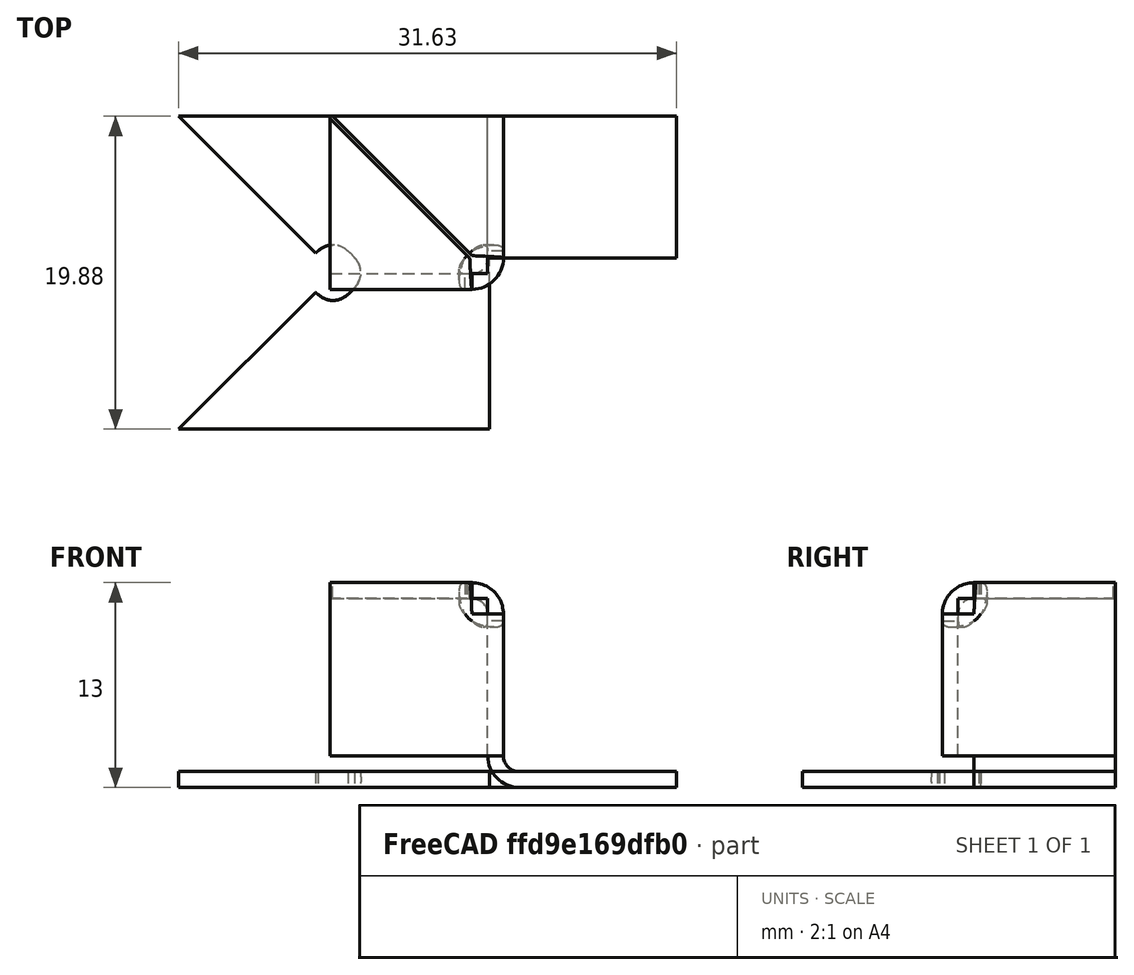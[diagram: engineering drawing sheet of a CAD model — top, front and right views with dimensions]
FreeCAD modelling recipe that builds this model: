
FCSTD DOCUMENT  (FreeCAD 0.19R23069 (Git))
Label: CornerRelief_test_none_native_SMWB
License: All rights reserved
LicenseURL: http://en.wikipedia.org/wiki/All_rights_reserved
objects: Part::FeaturePython×5, Sketcher::SketchObject×4, Part::Box×1, Part::Fillet×1, Part::Offset×1, Part::Feature×1, App::Part×1
note: 13 computed .brp shape members not serialized (recipe doc carries the construction recipe); baked Part::Feature solids carry a one-line shape summary decoded from their .brp

FEATURE [Part::Box] Box  label="Cube"
  AttacherType = Attacher::AttachEngine3D
  Height = 10
  Length = 10
  Width = 10
FEATURE [Part::FeaturePython] Relief  # WARN: FeaturePython — macro-defined, semantics opaque (R4)
  baseObject = -> Box [Vertex5]
  relief = 1
FEATURE [Sketcher::SketchObject] Sketch
  ExternalGeometry = -> [Relief]
  MapMode = 5
  Placement = pos=(0,0,10) rot=(0,0,1;0rad)
  Support = -> [Relief]
  sketch-geometry (7):
    g0: LineSegment [constr] StartX=9 StartY=1 StartZ=0 EndX=-4e-16 EndY=10 EndZ=0
    g1: LineSegment [constr] StartX=-0.0707107 StartY=9.92929 StartZ=0 EndX=0.0707107 EndY=10.0707 EndZ=0
    g2: LineSegment StartX=0.0707107 StartY=10.0707 StartZ=0 EndX=9.07071 EndY=1.07071 EndZ=0
    g3: LineSegment [constr] StartX=9.07071 StartY=1.07071 StartZ=0 EndX=8.92929 EndY=0.929289 EndZ=0
    g4: LineSegment StartX=8.92929 StartY=0.929289 StartZ=0 EndX=-0.0707107 EndY=9.92929 EndZ=0
    g5: ArcOfCircle CenterX=9 CenterY=1 CenterZ=0 NormalX=0 NormalY=0 NormalZ=1 AngleXU=0 Radius=0.1 StartAngle=3.92699 EndAngle=7.06858
    g6: ArcOfCircle CenterX=0 CenterY=10 CenterZ=0 NormalX=0 NormalY=0 NormalZ=1 AngleXU=0 Radius=0.1 StartAngle=0.785398 EndAngle=3.92699
  constraints (15):
    c: Coincident(g0,g-3)
    c: Coincident(g0,g-4)
    c: Perpendicular(g1,g2) = 4.71239
    c: Perpendicular(g2,g3) = 4.71239
    c: Perpendicular(g3,g4) = 4.71239
    c: Coincident(g1,g4)
    c: Symmetric(g1,g1,g0)
    c: Symmetric(g3,g3,g0)
    c: Distance(g1) = 0.2
    c: Coincident(g5,g0)
    c: Coincident(g5,g3)
    c: Coincident(g5,g2)
    c: Coincident(g6,g0)
    c: Coincident(g6,g1)
    c: Coincident(g6,g1)
FEATURE [Part::FeaturePython] XOR  # WARN: FeaturePython — macro-defined, semantics opaque (R4)
  Objects = -> [Sketch,Relief]
  Tolerance = 0
FEATURE [Part::FeaturePython] Facebinder  # WARN: FeaturePython — macro-defined, semantics opaque (R4)
  Area = 294.457
  Extrusion = 0
  Faces = -> [XOR]
  RemoveSplitter = false
  Sew = false
FEATURE [Part::Fillet] Fillet
  Base = -> Facebinder
  Edges = 3 edges r=1: [Edge2,Edge9,Edge11]
FEATURE [Part::Offset] Offset
  Fill = true
  Intersection = false
  Join = 0
  Mode = 0
  SelfIntersection = false
  Source = -> Fillet
  Value = 1
FEATURE [Part::FeaturePython] CornerRelief  # WARN: FeaturePython — macro-defined, semantics opaque (R4)
  ReliefSketch = 0
  Size = 2
  SizeRatio = 1.5
  XOffset = 0
  YOffset = 0
  baseObject = -> Offset [Edge49,Edge51]
  kfactor = 0.5
FEATURE [Part::FeaturePython] Bend  # WARN: FeaturePython — macro-defined, semantics opaque (R4)
  AutoMiter = true
  BendType = 0
  LengthList = [10]
  ReliefFactor = 0.7
  UseReliefFactor = false
  angle = 90
  baseObject = -> CornerRelief [Edge30]
  bendAList = [90]
  extend1 = 0
  extend2 = 0
  gap1 = 0
  gap2 = 0
  invert = false
  kfactor = 0.5
  length = 10
  miterangle1 = 0
  miterangle2 = 0
  offset = 0
  radius = 1
  reliefType = 0
  reliefd = 1
  reliefw = 0.8
  sketchflip = false
  sketchinvert = false
  unfold = false
FEATURE [Part::Feature] Unfold
  shape: bbox 31.63 x 19.89 x 1.1 mm, 17 faces (baked)
FEATURE [Sketcher::SketchObject] Unfold_Sketch
  sketch-geometry (15):
    g0: ArcOfCircle CenterX=0.408186 CenterY=0.293142 CenterZ=0 NormalX=0 NormalY=0 NormalZ=1 AngleXU=1.5708 Radius=2 StartAngle=2.40622 EndAngle=2.51171
    g1: LineSegment StartX=-0.933548 StartY=-1.19001 StartZ=0 EndX=-9.62849 EndY=-9.88496 EndZ=0
    g2: BSplineCurve PolesCount=15 KnotsCount=13 Degree=3 IsPeriodic=0
    g3: ArcOfCircle CenterX=-0.0630528 CenterY=0.293142 CenterZ=0 NormalX=0 NormalY=0 NormalZ=1 AngleXU=1.5708 Radius=2 StartAngle=3.77147 EndAngle=4.08251
    g4: BSplineCurve PolesCount=15 KnotsCount=13 Degree=3 IsPeriodic=0
    g5: ArcOfCircle CenterX=-0.0630528 CenterY=-0.178097 CenterZ=0 NormalX=0 NormalY=0 NormalZ=1 AngleXU=1.5708 Radius=2 StartAngle=5.34227 EndAngle=5.6533
    g6: BSplineCurve PolesCount=15 KnotsCount=13 Degree=3 IsPeriodic=0
    g7: BSplineCurve PolesCount=15 KnotsCount=13 Degree=3 IsPeriodic=0
    g8: ArcOfCircle CenterX=0.408186 CenterY=-0.178097 CenterZ=0 NormalX=0 NormalY=0 NormalZ=1 AngleXU=1.5708 Radius=2 StartAngle=0.629881 EndAngle=0.735377
    g9: LineSegment StartX=-9.62849 StartY=10 StartZ=0 EndX=-0.933548 EndY=1.30506 EndZ=0
    g10: LineSegment StartX=10.115 StartY=-9.88496 StartZ=0 EndX=-9.62849 EndY=-9.88496 EndZ=0
    g11: LineSegment StartX=10.115 StartY=-9.88496 StartZ=0 EndX=10.115 EndY=1 EndZ=0
    g12: LineSegment StartX=10.115 StartY=1 StartZ=0 EndX=22 EndY=1 EndZ=0
    g13: LineSegment StartX=22 StartY=1 StartZ=0 EndX=22 EndY=10 EndZ=0
    g14: LineSegment StartX=22 StartY=10 StartZ=0 EndX=-9.62849 EndY=10 EndZ=0
FEATURE [Sketcher::SketchObject] Unfold_Sketch_Outline
  sketch-geometry (15):
    g0: LineSegment StartX=10.115 StartY=-9.88496 StartZ=0 EndX=-9.62849 EndY=-9.88496 EndZ=0
    g1: LineSegment StartX=-0.933548 StartY=-1.19001 StartZ=0 EndX=-9.62849 EndY=-9.88496 EndZ=0
    g2: ArcOfCircle CenterX=0.408186 CenterY=0.293142 CenterZ=0 NormalX=0 NormalY=0 NormalZ=1 AngleXU=1.5708 Radius=2 StartAngle=2.40622 EndAngle=2.51171
    g3: BSplineCurve PolesCount=15 KnotsCount=13 Degree=3 IsPeriodic=0
    g4: ArcOfCircle CenterX=-0.0630528 CenterY=0.293142 CenterZ=0 NormalX=0 NormalY=0 NormalZ=1 AngleXU=1.5708 Radius=2 StartAngle=3.77147 EndAngle=4.08251
    g5: BSplineCurve PolesCount=15 KnotsCount=13 Degree=3 IsPeriodic=0
    g6: ArcOfCircle CenterX=-0.0630528 CenterY=-0.178097 CenterZ=0 NormalX=0 NormalY=0 NormalZ=1 AngleXU=1.5708 Radius=2 StartAngle=5.34227 EndAngle=5.6533
    g7: BSplineCurve PolesCount=15 KnotsCount=13 Degree=3 IsPeriodic=0
    g8: BSplineCurve PolesCount=15 KnotsCount=13 Degree=3 IsPeriodic=0
    g9: ArcOfCircle CenterX=0.408186 CenterY=-0.178097 CenterZ=0 NormalX=0 NormalY=0 NormalZ=1 AngleXU=1.5708 Radius=2 StartAngle=0.629881 EndAngle=0.735377
    g10: LineSegment StartX=-9.62849 StartY=10 StartZ=0 EndX=-0.933548 EndY=1.30506 EndZ=0
    g11: LineSegment StartX=22 StartY=10 StartZ=0 EndX=-9.62849 EndY=10 EndZ=0
    g12: LineSegment StartX=22 StartY=1 StartZ=0 EndX=22 EndY=10 EndZ=0
    g13: LineSegment StartX=10.115 StartY=1 StartZ=0 EndX=22 EndY=1 EndZ=0
    g14: LineSegment StartX=10.115 StartY=-9.88496 StartZ=0 EndX=10.115 EndY=1 EndZ=0
FEATURE [Sketcher::SketchObject] Unfold_Sketch_bends
  sketch-geometry (4):
    g0: LineSegment StartX=0.172567 StartY=-9.88496 StartZ=0 EndX=0.172567 EndY=-1.70686 EndZ=0
    g1: LineSegment StartX=10.115 StartY=0.0575222 StartZ=0 EndX=1.93695 EndY=0.0575222 EndZ=0
    g2: LineSegment StartX=0.172567 StartY=1.8219 StartZ=0 EndX=0.172567 EndY=10 EndZ=0
    g3: LineSegment StartX=11.0575 StartY=1 StartZ=0 EndX=11.0575 EndY=10 EndZ=0
FEATURE [App::Part] Part  label="unfold_set"
  Group = -> [Unfold,Unfold_Sketch,Unfold_Sketch_Outline,Unfold_Sketch_bends]
  Origin = -> Origin
  Placement = pos=(0,31,0) rot=(0,0,1;0rad)
